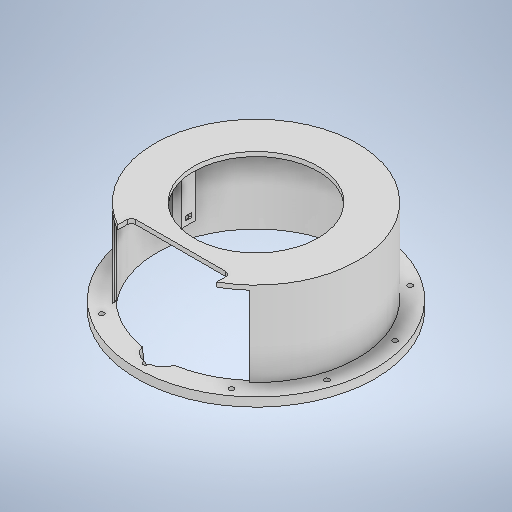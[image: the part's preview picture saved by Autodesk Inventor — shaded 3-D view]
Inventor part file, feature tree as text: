
AUTODESK INVENTOR PART (.ipt)
format: ipt  version: 2025.2 (Build 292293000, 293)  size: 445,440 bytes
history: native  units: in
note: dims shown in document units (in); Inventor stores cm internally (conversion verified against a paired STEP export)
features: sketch x10, extrude x10, plane x3, fillet x1
ambient origin geometry x8: Origin, YZ Plane, XZ Plane, XY Plane, X Axis, Y Axis, Z Axis, Center Point
bodies: Solid1 (feature_tree)
feature tree (24):
  sketch  "Sketch1"  dims[d5=0.0in d7=0.0in]
  extrude  "Extrusion1"  TaperAngle=0.0deg  [1 undecoded]
  extrude  "Extrusion2"  Depth=4.5276in
  extrude  "Extrusion7"  Depth=0.2165in
  extrude  "Extrusion34"  Depth=6.1024in
  sketch  "Sketch30"  dims[d272=3.937in d273=4.1535in d274=0.0in d285=3.937in]
  plane  "Work Plane19"
  plane  "Work Plane21"
  plane  "Work Plane22"
  extrude  "Extrusion36"  Depth=4.1535in TaperAngle=0.0deg
  fillet  "Fillet19"  Radius=3.937in
  extrude  "Extrusion37"  Depth=2.0812in TaperAngle=0.0deg
  extrude  "Extrusion38"  Depth=0.1969in
  sketch  "Sketch35"  dims[d293=0.1969in d294=0.1969in]
  extrude  "Extrusion40"  Depth=4.4094in
  extrude  "Extrusion41"  Depth=0.1969in
  extrude  "Extrusion42"  Depth=0.3937in TaperAngle=0.0deg
  sketch  "Sketch2"  dims[d18=0.0in d52=4.5276in]
  sketch  "Sketch Circular Pattern5"  dims[d264=9.8425in d265=0.2165in]
  sketch  "Sketch28"  dims[d266=3.937in d268=360.0deg d271=6.1024in]
  sketch  "Sketch31"  dims[d286=1.5748in d287=2.0812in d288=0.0in]
  sketch  "Sketch32"  dims[d289=3.5039in d290=0.1969in]
  sketch  "Sketch33"  dims[d291=4.4094in d292=1.5748in]
  sketch  "Sketch36"  dims[d295=3.3465in d296=0.3937in d297=0.0in d298=0.6299in d299=1.7717in d300=0.0in d301=2.9528in d308=6.378in d309=0.2805in d310=0.5906in d311=0.0in d312=6.8898in d313=5.5413in d314=0.2362in d315=0.1969in d316=0.0in d317=0.1969in d318=0.0in d326=0.315in d113=0.0197in d114=0.0344in d115=0.0197in d116=0.0344in d167=0.0197in d168=0.0344in d169=0.0197in d170=0.0344in d215=0.0197in d216=0.0344in d217=0.0197in d218=0.0344in d219=0.0in d220=0.0in d254=0.0197in d255=0.0344in d256=0.0197in d257=0.0344in]
note: 1 required parameter value undecoded (feature->parameter linkage not recoverable at this tier; creation-order binding heuristic only, values carry confidence <= 0.55)
